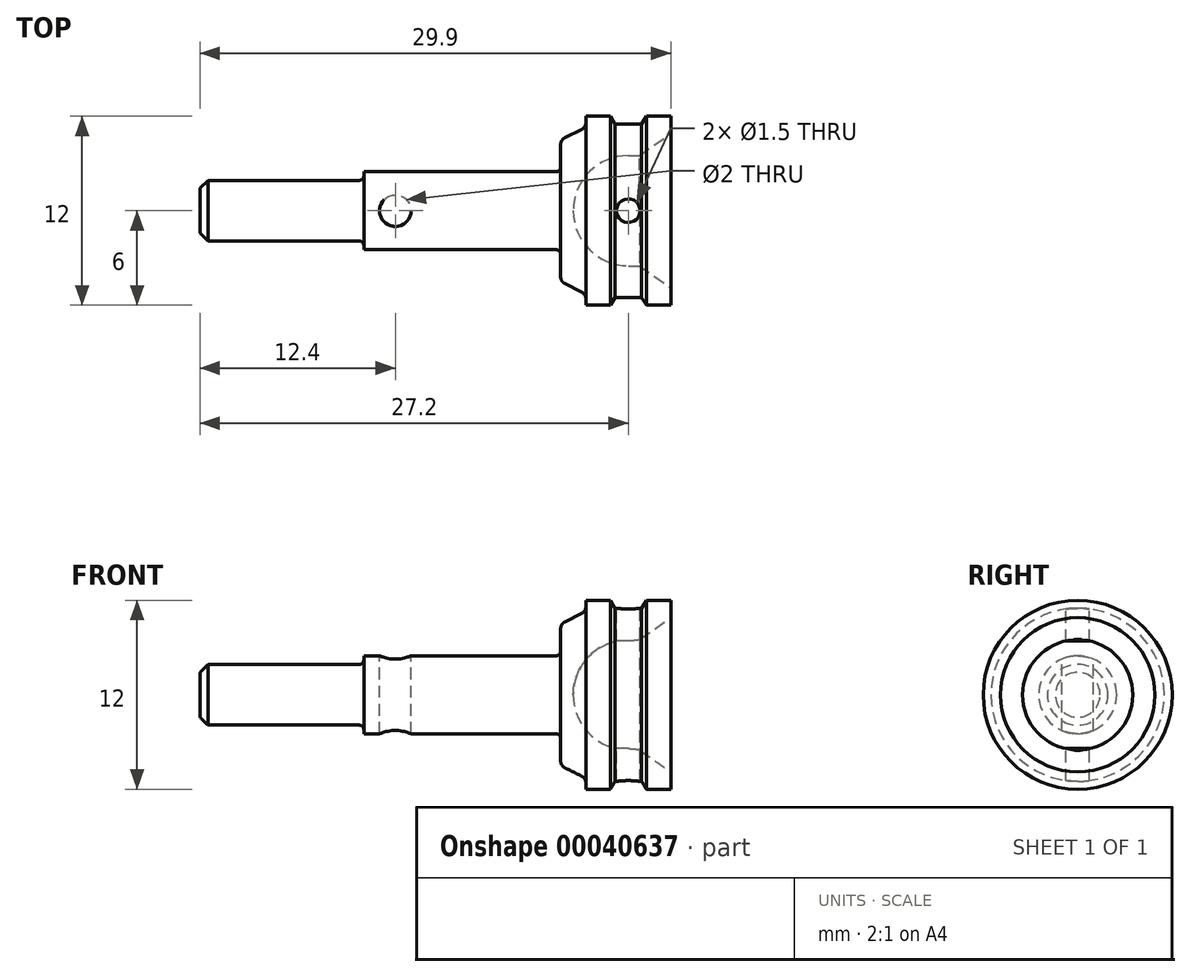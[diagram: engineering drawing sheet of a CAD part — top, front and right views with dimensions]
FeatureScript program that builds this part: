
annotation { "Feature Type Name" : "Feature", "Feature Type Description" : "" }
export const myFeature = defineFeature(function(context is Context, id is Id, definition is map)
    precondition{}
    {
        {
            var Q0;
            Q0=qCreatedBy(makeId("Top.planeOp"),FACE);
            var sketch = newSketch(context, id + "F0", { "sketchPlane" : qUnion([Q0])});
            skLineSegment(sketch, "E0", {"start": v(0, 50) * mm, "end": v(0, -50) * mm, "construction": true});
            skLineSegment(sketch, "E1", {"start": v(-50, 0) * mm, "end": v(50, 0) * mm, "construction": true});
            skSolve(sketch);
        }
        {
            var Q0;
            Q0=qCreatedBy(makeId("Front.planeOp"),FACE);
            var sketch = newSketch(context, id + "F1", { "sketchPlane" : qUnion([Q0])});
            skLineSegment(sketch, "E2", {"start": v(0, 50) * mm, "end": v(0, -50) * mm, "construction": true});
            skSolve(sketch);
        }
        {
            var Q0;
            Q0=qCreatedBy(makeId("Front.planeOp"),FACE);
            var sketch = newSketch(context, id + "F2", { "sketchPlane" : qUnion([Q0])});
            skArc(sketch, "E3", {"start": v(0, 3.5) * mm, "mid": v(-2.47, 2.47) * mm, "end": v(-3.5, 0) * mm});
            skLineSegment(sketch, "E4", {"start": v(0, 3.5) * mm, "end": v(5, 3.5) * mm});
            skLineSegment(sketch, "E5", {"start": v(5, 3.5) * mm, "end": v(5, 0) * mm});
            skLineSegment(sketch, "E6", {"start": v(5, 0) * mm, "end": v(-3.5, 0) * mm});
            skLineSegment(sketch, "E7", {"start": v(-1.6, 1.92) * mm, "end": v(1.6, -1.92) * mm, "construction": true});
            skLineSegment(sketch, "E8", {"start": v(-3.89, 0) * mm, "end": v(0.27, 3.49) * mm, "construction": true});
            skArc(sketch, "E9", {"start": v(0, 3.5) * mm, "mid": v(0.13, 3.5) * mm, "end": v(0.27, 3.49) * mm, "construction": true});
            skLineSegment(sketch, "E10", {"start": v(0.27, 3.49) * mm, "end": v(3.88, 5.21) * mm, "construction": true});
            skLineSegment(sketch, "E11.0", {"start": v(-50, 0) * mm, "end": v(50, 0) * mm, "construction": true});
            skSolve(sketch);
        }
        {
            var Q0;
            Q0=qCreatedBy(makeId("Front.planeOp"),FACE);
            var sketch = newSketch(context, id + "F3", { "sketchPlane" : qUnion([Q0])});
            skLineSegment(sketch, "E12", {"start": v(-2.7, 6) * mm, "end": v(2.7, 6) * mm});
            skLineSegment(sketch, "E13", {"start": v(2.7, 6) * mm, "end": v(2.7, 0) * mm});
            skLineSegment(sketch, "E14", {"start": v(-27.2, 0) * mm, "end": v(2.7, 0) * mm});
            skLineSegment(sketch, "E15", {"start": v(-16.8, 1.93) * mm, "end": v(-27.2, 1.93) * mm});
            skLineSegment(sketch, "E16", {"start": v(-16.8, 2.48) * mm, "end": v(-4.6, 2.48) * mm});
            skLineSegment(sketch, "E17", {"start": v(-16.8, 2.47) * mm, "end": v(-16.8, 1.93) * mm});
            skLineSegment(sketch, "E18", {"start": v(-27.2, 1.93) * mm, "end": v(-27.2, 0) * mm});
            skLineSegment(sketch, "E19", {"start": v(-4.3, 2.77) * mm, "end": v(-4.3, 4.5) * mm});
            skLineSegment(sketch, "E20", {"start": v(-2.7, 6) * mm, "end": v(-2.7, 5.3) * mm});
            skLineSegment(sketch, "E21", {"start": v(-2.7, 5.3) * mm, "end": v(-4.3, 4.5) * mm});
            skPoint(sketch, "E22.visualSharp", {"position": v(-4.3, 2.48) * mm});
            skArc(sketch, "E22.filletArc", {"start": v(-4.6, 2.48) * mm, "mid": v(-4.39, 2.56) * mm, "end": v(-4.3, 2.77) * mm});
            skLineSegment(sketch, "E23.0", {"start": v(-50, 0) * mm, "end": v(50, 0) * mm, "construction": true});
            skSolve(sketch);
        }
        {
            var Q0;
            Q0=makeQuery(id+"F3.imprint","IMPRINT",FACE,{"disambiguationData":[TD([[makeQuery(id+"F3.imprint","IMPRINT",EDGE,{"derivedFrom":sQuery(id+"F3.wireOp",EDGE,"E12")}),-1.0]])]});
            var Q1;
            Q1=sQuery(id+"F0.wireOp",EDGE,"E1");
            revolve(context, id + "F4", {"entities" : qUnion([Q0]), "axis" : qUnion([Q1]), "revolveType" : RevolveType.FULL});
        }
        {
            var Q0;
            Q0=qSketchRegion(id+"F2",true);
            var Q1;
            Q1=sQuery(id+"F3.wireOp",EDGE,"E23.0");
            revolve(context, id + "F5", {"operationType" : NewBodyOperationType.REMOVE, "entities" : qUnion([Q0]), "axis" : qUnion([Q1]), "revolveType" : RevolveType.FULL, "oppositeDirection" : true});
        }
        {
            var Q0;
            Q0=qCreatedBy(makeId("Front.planeOp"),FACE);
            var sketch = newSketch(context, id + "F6", { "sketchPlane" : qUnion([Q0])});
            skLineSegment(sketch, "E24", {"start": v(-1.14, 6) * mm, "end": v(-0.85, 5.5) * mm});
            skLineSegment(sketch, "E25", {"start": v(-0.85, 5.5) * mm, "end": v(0.85, 5.5) * mm});
            skLineSegment(sketch, "E26.MirrorCS", {"start": v(1.14, 6) * mm, "end": v(0.85, 5.5) * mm});
            skLineSegment(sketch, "E27.MirrorCS", {"start": v(-0.85, -5.5) * mm, "end": v(0.85, -5.5) * mm, "construction": true});
            skLineSegment(sketch, "E28", {"start": v(-1.14, 6) * mm, "end": v(1.14, 6) * mm});
            skSolve(sketch);
        }
        {
            var Q0;
            Q0=qSketchRegion(id+"F6",true);
            var Q1;
            Q1=sQuery(id+"F0.wireOp",EDGE,"E1");
            revolve(context, id + "F7", {"operationType" : NewBodyOperationType.REMOVE, "entities" : qUnion([Q0]), "axis" : qUnion([Q1]), "revolveType" : RevolveType.FULL, "oppositeDirection" : true});
        }
        {
            var Q0;
            Q0=qCreatedBy(makeId("Top.planeOp"),FACE);
            var sketch = newSketch(context, id + "F8", { "sketchPlane" : qUnion([Q0])});
            skCircle(sketch, "E29", {"center": v(0, 0) * mm, "radius": 0.75 * mm});
            skCircle(sketch, "E30", {"center": v(-14.8, 0) * mm, "radius": 1 * mm});
            skSolve(sketch);
        }
        {
            var Q0;
            Q0=qSketchRegion(id+"F8",true);
            extrude(context, id + "F9", {"entities" : qUnion([Q0]), "operationType" : NewBodyOperationType.REMOVE, "endBound" : BoundingType.THROUGH_ALL, "oppositeDirection" : true, "depth" : 20 * mm, "hasSecondDirection" : true, "secondDirectionBound" : SecondDirectionBoundingType.THROUGH_ALL, "secondDirectionOppositeDirection" : false, "secondDirectionDepth" : 25 * mm});
        }
        {
            var Q0;
            Q0=makeQuery(id+"F5.boolean.opBoolean","INTERSECT",EDGE,{"derivedFrom":[makeQuery(id+"F4.opRevolve","SWEPT_FACE",FACE,{"disambiguationData":[OSD([sQuery(id+"F3.wireOp",EDGE,"E13")])]}),makeQuery(id+"F5.opRevolve","SWEPT_FACE",FACE,{"disambiguationData":[OSD([sQuery(id+"F2.wireOp",EDGE,"E4")])]})]});
            chamfer(context, id + "F10", {"entities" : qUnion([Q0]), "chamferType" : ChamferType.OFFSET_ANGLE, "width" : 2 * mm, "oppositeDirection" : true, "angle" : 35 * degree, "tangentPropagation" : true});
        }
        {
            var Q0;
            Q0=makeQuery(id+"F4.opRevolve","SWEPT_EDGE",EDGE,{"disambiguationData":[OSD([sQuery(id+"F3.wireOp",EDGE,"E15"),sQuery(id+"F3.wireOp",EDGE,"E18")])]});
            chamfer(context, id + "F11", {"entities" : qUnion([Q0]), "width" : 0.5 * mm, "tangentPropagation" : true});
        }
        {
            var Q0;
            Q0=makeQuery(id+"F4.opRevolve","SWEPT_EDGE",EDGE,{"disambiguationData":[OSD([sQuery(id+"F3.wireOp",EDGE,"E19"),sQuery(id+"F3.wireOp",EDGE,"E21")])]});
            var Q1;
            Q1=makeQuery(id+"F4.opRevolve","SWEPT_EDGE",EDGE,{"disambiguationData":[OSD([sQuery(id+"F3.wireOp",EDGE,"E20"),sQuery(id+"F3.wireOp",EDGE,"E21")])]});
            fillet(context, id + "F12", {"entities" : qUnion([Q0, Q1]), "radius" : 0.5 * mm, "tangentPropagation" : true, "allowEdgeOverflow" : false});
        }
        {
            var Q0;
            Q0=makeQuery(id+"F4.opRevolve","SWEPT_EDGE",EDGE,{"disambiguationData":[OSD([sQuery(id+"F3.wireOp",EDGE,"E15"),sQuery(id+"F3.wireOp",EDGE,"E17")])]});
            fillet(context, id + "F13", {"entities" : qUnion([Q0]), "radius" : 0.3 * mm, "tangentPropagation" : true, "allowEdgeOverflow" : false});
        }
    });
